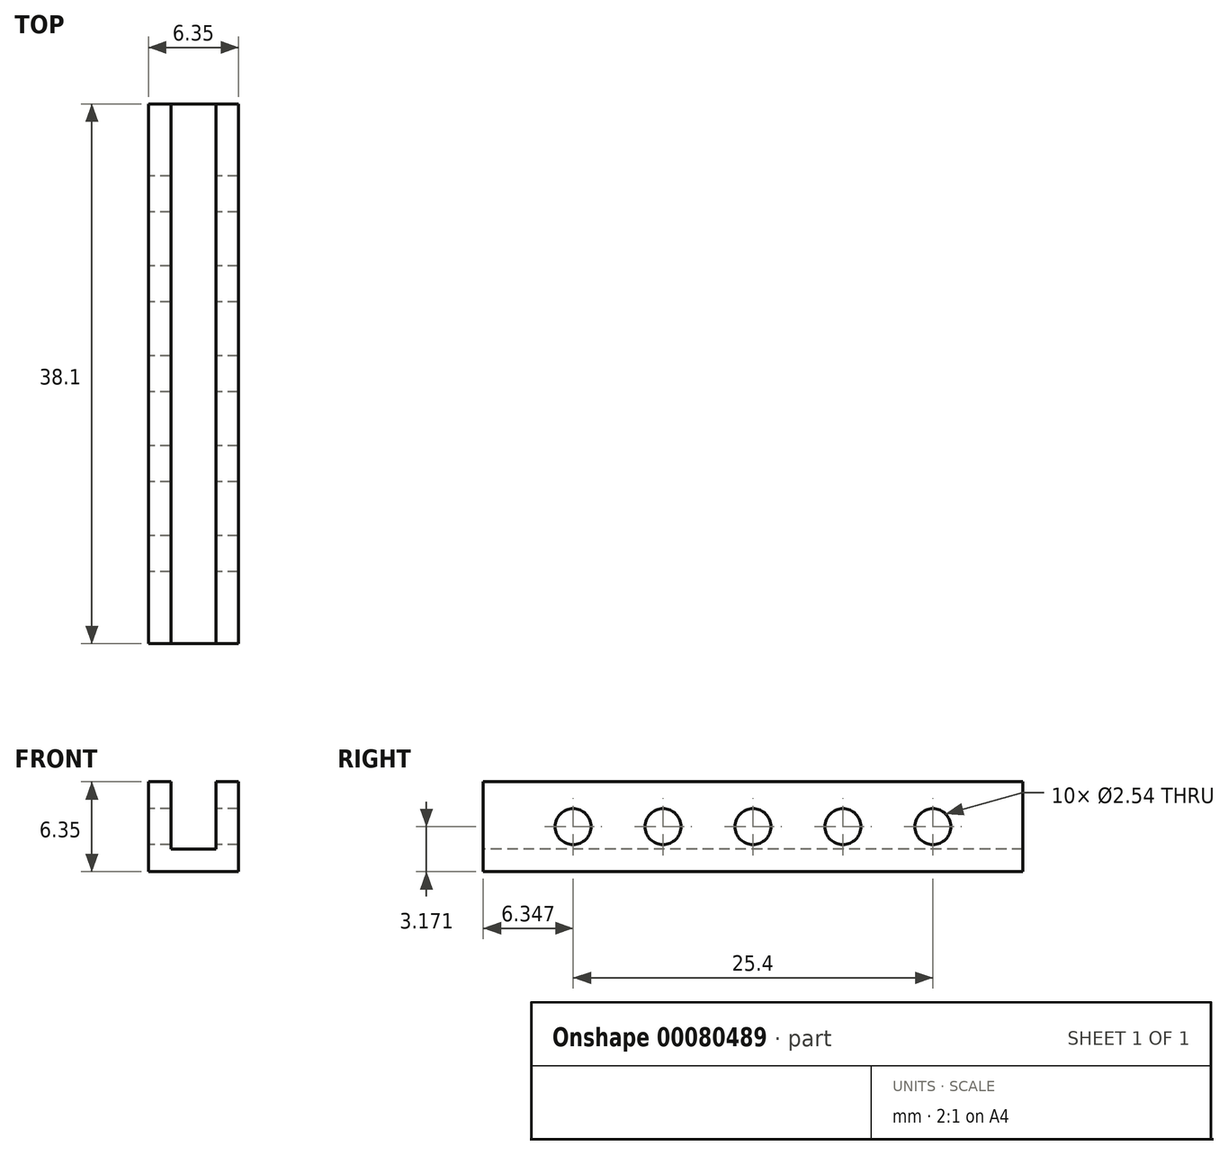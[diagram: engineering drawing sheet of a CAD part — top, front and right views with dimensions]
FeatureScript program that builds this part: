
annotation { "Feature Type Name" : "Feature", "Feature Type Description" : "" }
export const myFeature = defineFeature(function(context is Context, id is Id, definition is map)
    precondition{}
    {
        {
            var Q0;
            Q0=qCreatedBy(makeId("Right.planeOp"),FACE);
            var sketch = newSketch(context, id + "F0", { "sketchPlane" : qUnion([Q0])});
            skLineSegment(sketch, "E0.bottom", {"start": v(-4.94, -68.91) * mm, "end": v(-43.04, -68.91) * mm});
            skLineSegment(sketch, "E0.top", {"start": v(-4.94, -75.26) * mm, "end": v(-43.04, -75.26) * mm});
            skLineSegment(sketch, "E0.left", {"start": v(-4.94, -68.91) * mm, "end": v(-4.94, -75.26) * mm});
            skLineSegment(sketch, "E0.right", {"start": v(-43.04, -68.91) * mm, "end": v(-43.04, -75.26) * mm});
            skLineSegment(sketch, "E1.0", {"start": v(-4.94, -72.09) * mm, "end": v(-43.04, -72.09) * mm});
            skLineSegment(sketch, "E2.0", {"start": v(-11.3, -68.91) * mm, "end": v(-11.3, -75.26) * mm});
            skLineSegment(sketch, "E3.0", {"start": v(-17.64, -68.91) * mm, "end": v(-17.64, -75.26) * mm});
            skLineSegment(sketch, "E4.0", {"start": v(-24, -68.91) * mm, "end": v(-24, -75.26) * mm});
            skLineSegment(sketch, "E5.0", {"start": v(-30.34, -68.91) * mm, "end": v(-30.34, -75.26) * mm});
            skLineSegment(sketch, "E6.0", {"start": v(-36.7, -68.91) * mm, "end": v(-36.7, -75.26) * mm});
            skCircle(sketch, "E7", {"center": v(-11.3, -72.09) * mm, "radius": 1.27 * mm});
            skCircle(sketch, "E8", {"center": v(-17.64, -72.09) * mm, "radius": 1.27 * mm});
            skCircle(sketch, "E9", {"center": v(-24, -72.09) * mm, "radius": 1.27 * mm});
            skCircle(sketch, "E10", {"center": v(-30.34, -72.09) * mm, "radius": 1.27 * mm});
            skCircle(sketch, "E11", {"center": v(-36.7, -72.09) * mm, "radius": 1.27 * mm});
            skSolve(sketch);
        }
        {
            var Q0;
            Q0 = qSketchRegion(id + "F0", true);
            extrude(context, id + "F1", {"entities" : qUnion([Q0]), "depth" : 6.35 * mm});
        }
        {
            var Q0;
            Q0=makeQuery(id+"F1.opExtrude","SWEPT_FACE",FACE,{"disambiguationData":[OSD([sQuery(id+"F0.wireOp",EDGE,"E0.right")])]});
            var sketch = newSketch(context, id + "F2", { "sketchPlane" : qUnion([Q0])});
            skLineSegment(sketch, "E12.0", {"start": v(1.59, -68.9) * mm, "end": v(1.59, -73.68) * mm});
            skLineSegment(sketch, "E12.2", {"start": v(4.76, -73.68) * mm, "end": v(4.76, -68.92) * mm});
            skLineSegment(sketch, "E12.3", {"start": v(1.59, -73.68) * mm, "end": v(4.76, -73.68) * mm});
            skLineSegment(sketch, "E13", {"start": v(4.76, -68.92) * mm, "end": v(1.59, -68.9) * mm});
            skSolve(sketch);
        }
        {
            var Q0;
            {var subQ1=sQuery(id+"F2.wireOp",EDGE,"E12.2");Q0=makeQuery(id+"F2.imprint","IMPRINT",FACE,{"disambiguationData":[TD([[makeQuery(id+"F2.imprint","IMPRINT",EDGE,{"derivedFrom":subQ1}),1.0]])]});}
            extrude(context, id + "F3", {"entities" : qUnion([Q0]), "operationType" : NewBodyOperationType.REMOVE, "endBound" : BoundingType.THROUGH_ALL, "oppositeDirection" : true, "depth" : 25.4 * mm});
        }
    });
